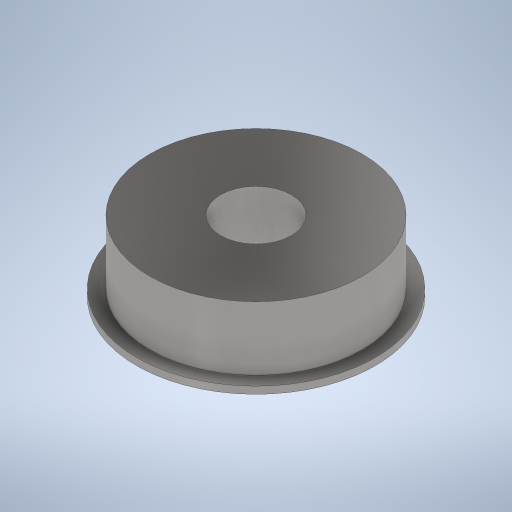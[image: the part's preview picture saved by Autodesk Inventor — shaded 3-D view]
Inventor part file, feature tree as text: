
AUTODESK INVENTOR PART (.ipt)
format: ipt  version: 2024 (Build 280153000, 153)  size: 250,880 bytes
history: native  units: mm
features: extrude x3
ambient origin geometry x8: Origin, YZ Plane, XZ Plane, XY Plane, X Axis, Y Axis, Z Axis, Center Point
bodies: Solid1 (feature_tree)
feature tree (3):
  extrude  "Extrusion1"  Depth=27.0mm
  extrude  "Extrusion2"  Depth=24.0mm
  extrude  "Extrusion3"  Depth=8.0mm
